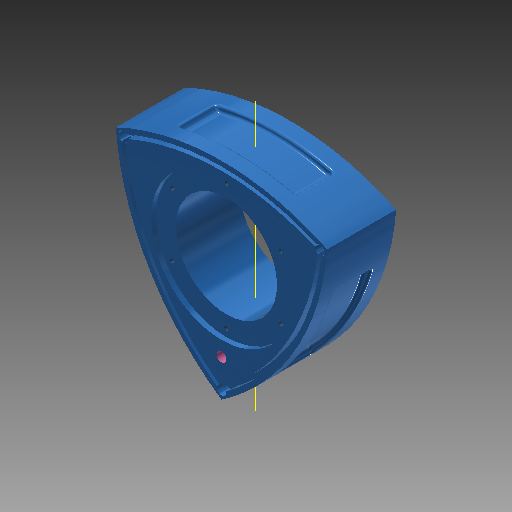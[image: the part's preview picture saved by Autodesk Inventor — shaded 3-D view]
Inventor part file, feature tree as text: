
AUTODESK INVENTOR PART (.ipt)
format: ipt  version: 2019 (Build 230136000, 136)  size: 522,752 bytes
history: native  units: mm (DEFAULTED — no unit token found)
features: sketch x9, extrude x7, pattern_circular x5, fillet x2, hole x2, plane x1, mirror x1, projected_geometry x1
ambient origin geometry x8: Origin, YZ Plane, XZ Plane, XY Plane, X Axis, Y Axis, Z Axis, Center Point
bodies: Solid1 (feature_tree)
feature tree (28):
  extrude  "Extrusion1"  TaperAngle=0.0deg  [1 undecoded]
  plane  "Work Plane1"
  extrude  "Extrusion3"  Depth=130.0mm
  extrude  "Extrusion4"  Depth=56.0mm TaperAngle=0.0deg
  extrude  "Extrusion5"  Depth=4.0mm TaperAngle=0.0deg
  fillet  "Fillet1"  Radius=198.0mm
  fillet  "Fillet2"  Radius=8.0mm
  pattern_circular  "Circular Pattern1"  Count=16  [1 undecoded]
  pattern_circular  "Circular Pattern2"  Count=20  [1 undecoded]
  hole  "Hole3"  [1 undecoded]
  pattern_circular  "Circular Pattern3"  [2 undecoded]
  extrude  "Extrusion6"  Depth=30.0mm TaperAngle=0.0deg
  hole  "Hole4"  [1 undecoded]
  mirror  "Mirror1"
  extrude  "Extrusion7"  Depth=2.0mm
  pattern_circular  "Circular Pattern4"  Count=3 Angle=360.0deg
  extrude  "Extrusion8"  Depth=30.0mm TaperAngle=360.0deg
  pattern_circular  "Circular Pattern5"  [2 undecoded]
  sketch  "Sketch1"  dims[d0=0.0mm d1=0.0mm]
  sketch  "Sketch3"  dims[d7=130.0mm d9=82.0mm]
  sketch  "Sketch4"  dims[d10=30.0deg d11=56.0mm d12=0.0mm]
  sketch  "Sketch5"  dims[d26=114.0mm d27=4.0mm d28=0.0mm d29=198.0mm d30=8.0mm]
  sketch  "Sketch7"  dims[d32=0.0mm]
  sketch  "Sketch8"  dims[d33=10.0mm d34=0.0mm d35=160.0mm]
  sketch  "Sketch9"  dims[d36=95.0mm d37=200.0mm]
  projected_geometry  "Projected Loop1"
  sketch  "Sketch10"  dims[d38=115.0mm d39=25.0mm]
  sketch  "Sketch11"  dims[d40=73.0mm d41=5.0mm d42=30.0mm d43=0.0mm d44=2.0mm d45=2.0mm d46=30.0mm d47=360.0deg d49=30.0mm d50=360.0deg d60=51.0mm d61=3.242mm d62=8.0mm d63=4.0mm d64=2.0mm d65=90.0deg d66=11.8mm d67=20.594885mm d68=60.0mm d69=360.0deg d71=4.0mm d72=3.0mm d73=7.0mm d74=0.0mm d75=7.0mm d76=0.0mm d77=6.062178mm d78=3.5mm d79=6.062178mm d80=8.0mm d81=6.0mm d82=4.0mm d83=2.0mm d84=90.0deg d85=8.0mm d86=0.0mm d87=184.0mm d88=184.0mm d89=59.892157mm d90=2.0mm d91=30.0mm d92=0.0mm d93=30.0mm d94=360.0deg d96=57.0mm d97=49.0mm d98=0.872665mm d99=9.075712mm d100=30.0mm d101=0.0mm d102=30.0mm d103=360.0deg]
note: 9 required parameter values undecoded (feature->parameter linkage not recoverable at this tier; creation-order binding heuristic only, values carry confidence <= 0.55)
